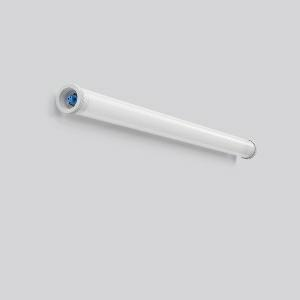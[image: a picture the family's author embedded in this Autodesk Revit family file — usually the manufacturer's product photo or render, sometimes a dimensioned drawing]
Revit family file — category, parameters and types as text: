
# Revit family: planox_tube_601071_002_730hf_5a42
name_source: partatom
category: Lighting Fixtures
units: mm (PartAtom-declared; Revit-internal decimal feet)

## family parameters
Cut with Voids When Loaded = No
Host = Face
Light Source = No
Part Type = Normal
Room Calculation Point = No
Round Connector Dimension = Use Diameter
Shared = No

## types (1)
- PLANOX TUBE (1 x LED Modul 840, 5350 lm, 4000)
    Apparent Load = 39 VA
    CIE Flux Codes = 42 71 89 90 100
    Color Rendering = 80
    Color Temperature = 4000
    Default Elevation = 1800 mm
    Description = Series: PLANOX TUBE
Robust protective tube luminaire for tough requirements. Rack made of sheet steel, white powder coated. End caps made of plastic (polyamide) grey. Diffuser made of plastic (polycarbonate), opal, shockproof. Symmetrical light distribution. Homogeneous light distribution. With accessories for wall, ceiling or pendant mounting. Mounting set must be ordered separately. Luminaire with limited surface temperature in accordance with EN 60598-2-24 for use in environments in which a deposit of conductive dust on the luminaire can be expected. Qualified for use in the food and drink industry. Suitable for lighting in public car parks and public off-street parking spaces according to DIN 67528. Environmentally friendly and resource-saving due to replaceable components. 
Colour: white
Diameter: 78 mm
Length: 1349 mm
Lamp: LED
Socket: without socket
Colour temperature: 4000K
Colour rendering index (CRI): 83
System power: 39 W
Rated luminous flux: 5350 lm
Luminous efficiency: 137 lm/W
Control gear: Dimmable Bluetooth converter
Protection class: I
Type of protection: IP 67
    Height = 0 mm  [stored 0 ft]
    Lamp = 1 x LED Modul 840
    Lamp Light Flux = 5350 lm
    Lamp count = 1
    Length = 1349 mm
    Lifetime = 50000 h
    Luminous efficacy = 137 lm/W
    Manufacturer = RZB
    ModVariant = No
    Model = 601071.002.730HF
    Mounting Place = Ceiling, Wall
    Mounting Type = Surface mounted
    Number of Poles = 1
    OnlyDefault = Yes
    Power Factor = 1
    Product Name = PLANOX TUBE
    Product group = Surface mounted luminaires for moist/humid enviroments
    ProductGroupID = 308
    Protection Class = Protection class I
    Protection Degree = Degree of protection
    RLX_Detail_Level = 1
    RLX_Emergency_Light_Flux = 0 lm
    RLX_Emergency_Type = 0
    RLX_Emergency_Type_DB = No
    RlxData = <blob elided: 33609 chars, md5=083fa974>
    Socket = socket
    Standby Power = 0 W
    System Light Flux = 5350 lm
    System Power = 39 W
    Type Comments = Product without accessories
    Type Image = 601071.002.jpg
    URL = http://relux.com
    VarID = ---
    Voltage = 230 V
    Voltage Range = 220-240 V
    Weight = 0.00 kg
    Width = 0 mm  [stored 0 ft]

note: [stored X ft] marks values corroborated as IEEE doubles in the binary element streams (Revit-internal decimal feet)

## geometry (parser evidence)
native form markers: Blend x4, Sweep x13
no freeform markers — native parametric forms only
